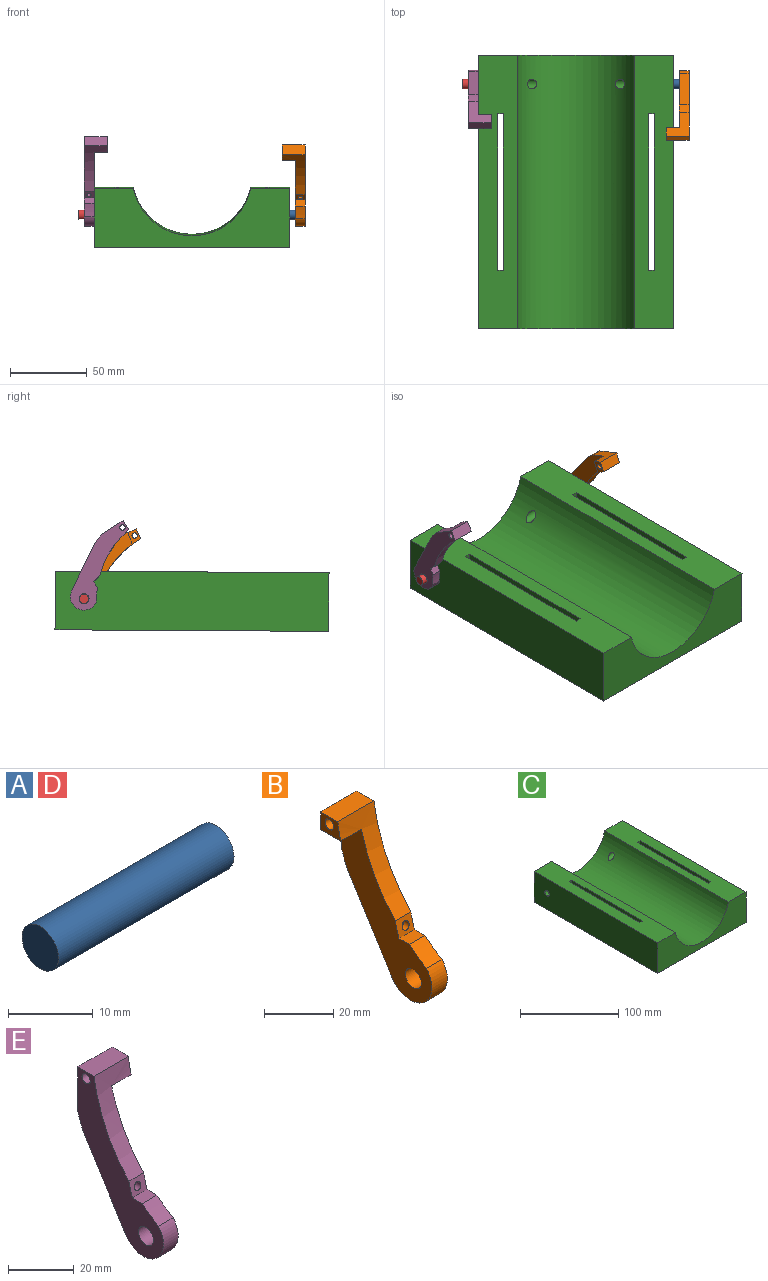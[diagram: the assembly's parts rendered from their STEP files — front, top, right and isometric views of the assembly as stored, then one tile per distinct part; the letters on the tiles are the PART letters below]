
ASSEMBLY  parts=5 mates=8
PART A: 3 faces, bbox 29.2x6.1x6.1 mm
  f0: cylinder r=3.05mm len=29.21mm, axis (1,0,0), area 559.4mm2, adj f1,f2
  f1: plane 6.1x6.1mm, normal (-1,0,0), area 29.2mm2, adj f0
  f2: plane 6.1x6.1mm, normal (1,0,0), area 29.2mm2, adj f0
PART B: 17 faces, bbox 14.8x36.9x56.7 mm
  f0: plane 50.49x36.92mm, normal (-1,0,0), area 667.1mm2, adj f1,f2,f3,f4,f5,f6,f8,f9
  f1: plane 29.6x18.48mm, normal (0,0.85,-0.53), area 221.6mm2, adj f0,f2,f9,f11
  f2: cylinder r=8.73mm len=16.13mm, axis (-1,0,0), area 183mm2, adj f0,f1,f3,f11
  f3: cylinder r=58.9mm len=6.98mm, axis (-1,0,0), area 54.4mm2, adj f0,f2,f4,f11
  f4: plane 6.35x4.29mm, normal (0,0,1), area 27.2mm2, adj f0,f3,f5,f11
  f5: plane 6.35x5.48mm, normal (0,-0.96,0.26), area 29.8mm2, adj f0,f4,f6,f11,f15
  f6: cylinder r=58.9mm len=31.78mm, axis (-1,0,0), area 280.3mm2, adj f0,f5,f7,f11,f12,f13
  f7: plane 14.81x6.96mm, normal (0,0,1), area 103.1mm2, adj f6,f8,f11,f13
  f8: plane 16.75x14.81mm, normal (0,1,0), area 159mm2, adj f0,f7,f9,f11,f12,f13
  f9: cylinder r=54.94mm len=6.35mm, axis (-1,0,0), area 42.4mm2, adj f0,f1,f8,f11
  f10: cylinder r=3.25mm len=6.5mm, axis (-1,0,0), area 129.7mm2, adj f0,f11
  f11: plane 56.71x36.92mm, normal (1,0,0), area 704.2mm2, adj f1,f2,f3,f4,f5,f6,f7,f8
  f12: plane 8.46x8.17mm, normal (0,0,-1), area 69.1mm2, adj f0,f6,f8,f13
  f13: plane 8.17x6.22mm, normal (-1,0,0), area 37mm2, adj f6,f7,f8,f12,f14
  f14: cylinder r=1.76mm len=14.81mm, axis (-1,0,0), area 163.6mm2, adj f11,f13
  f15: cylinder r=1.4mm len=2.79mm, axis (0,-1,0), area 17.3mm2, adj f5,f16
  f16: plane 2.79x2.79mm, normal (0,-1,0), area 6.1mm2, adj f15
PART C: 18 faces, bbox 127x177.8x38.1 mm
  f0: plane 177.8x127mm, normal (0,0,-1), area 21835mm2, adj f2,f3,f4,f6,f7,f8,f9,f12
  f1: plane 177.8x25.4mm, normal (0,0,1), area 4143.3mm2, adj f2,f3,f4,f5,f6,f7,f8,f9
  f2: plane 127x38.1mm, normal (0,-1,0), area 3099mm2, adj f0,f1,f4,f5,f11,f12
  f3: plane 127x38.1mm, normal (0,1,0), area 3099mm2, adj f0,f1,f4,f5,f11,f12
  f4: plane 177.8x38.1mm, normal (-1,0,0), area 6742.5mm2, adj f0,f1,f2,f3,f10
  f5: cylinder r=39.02mm len=177.8mm, axis (0,-1,0), area 18691.8mm2, adj f1,f2,f3,f10,f11,f17
  f6: plane 38.1x3.67mm, normal (0,-1,0), area 139.8mm2, adj f0,f1,f7,f9
  f7: plane 101.6x38.1mm, normal (1,0,0), area 3871mm2, adj f0,f1,f6,f8
  f8: plane 38.1x3.67mm, normal (0,1,0), area 139.8mm2, adj f0,f1,f7,f9
  f9: plane 101.6x38.1mm, normal (-1,0,0), area 3871mm2, adj f0,f1,f6,f8
  f10: cylinder r=3.17mm len=37.9mm, axis (1,0,0), area 694.5mm2, adj f4,f5
  f11: plane 177.8x25.4mm, normal (0,0,1), area 4143.3mm2, adj f2,f3,f5,f12,f13,f14,f15,f16
  f12: plane 177.8x38.1mm, normal (1,0,0), area 6742.5mm2, adj f0,f2,f3,f11,f17
  f13: plane 38.1x3.67mm, normal (0,-1,0), area 139.8mm2, adj f0,f11,f14,f16
  f14: plane 101.6x38.1mm, normal (-1,0,0), area 3871mm2, adj f0,f11,f13,f15
  f15: plane 38.1x3.67mm, normal (0,1,0), area 139.8mm2, adj f0,f11,f14,f16
  f16: plane 101.6x38.1mm, normal (1,0,0), area 3871mm2, adj f0,f11,f13,f15
  f17: cylinder r=3.17mm len=37.9mm, axis (-1,0,0), area 694.5mm2, adj f5,f12
PART D: same geometry as A
PART E: 17 faces, bbox 14.8x36.9x56.7 mm
  f0: plane 50.49x36.92mm, normal (1,0,0), area 667.1mm2, adj f1,f2,f3,f4,f5,f6,f8,f9
  f1: plane 29.6x18.48mm, normal (0,0.85,-0.53), area 221.6mm2, adj f0,f2,f9,f11
  f2: cylinder r=8.73mm len=16.13mm, axis (1,0,0), area 183mm2, adj f0,f1,f3,f11
  f3: cylinder r=58.9mm len=6.98mm, axis (1,0,0), area 54.4mm2, adj f0,f2,f4,f11
  f4: plane 6.35x4.29mm, normal (0,0,1), area 27.2mm2, adj f0,f3,f5,f11
  f5: plane 6.35x5.48mm, normal (0,-0.96,0.26), area 29.8mm2, adj f0,f4,f6,f11,f15
  f6: cylinder r=58.9mm len=31.78mm, axis (1,0,0), area 280.3mm2, adj f0,f5,f7,f11,f12,f13
  f7: plane 14.81x6.96mm, normal (0,0,1), area 103.1mm2, adj f6,f8,f11,f13
  f8: plane 16.75x14.81mm, normal (0,1,0), area 159mm2, adj f0,f7,f9,f11,f12,f13
  f9: cylinder r=54.94mm len=6.35mm, axis (1,0,0), area 42.4mm2, adj f0,f1,f8,f11
  f10: cylinder r=3.25mm len=6.5mm, axis (1,0,0), area 129.7mm2, adj f0,f11
  f11: plane 56.71x36.92mm, normal (-1,0,0), area 704.2mm2, adj f1,f2,f3,f4,f5,f6,f7,f8
  f12: plane 8.46x8.17mm, normal (0,0,-1), area 69.1mm2, adj f0,f6,f8,f13
  f13: plane 8.17x6.22mm, normal (1,0,0), area 37mm2, adj f6,f7,f8,f12,f14
  f14: cylinder r=1.76mm len=14.81mm, axis (1,0,0), area 163.6mm2, adj f11,f13
  f15: cylinder r=1.4mm len=2.79mm, axis (0,-1,0), area 17.3mm2, adj f5,f16
  f16: plane 2.79x2.79mm, normal (0,-1,0), area 6.1mm2, adj f15
PLACE A rot(axis=(0,0.8,-0.6),180deg) t=(129.31,51.74,68.67)mm
PLACE B rot(axis=(1,0,0),68.1deg) t=(23.6,44.91,-64.25)mm
PLACE C rot(axis=(1,0,0),0.3deg) t=(9.99,-0.05,-19.54)mm
PLACE D rot(axis=(0,1,0),180deg) t=(11.2,0.01,2.22)mm fixed
PLACE E rot(axis=(1,0,0),57.8deg) t=(0,33.58,-58.69)mm
MATE cylindrical A.f0 <-> B.f10  axis (1,0,0) through (83.65,69.99,1.1)mm
MATE cylindrical E.f10 <-> C.f10  axis (-1,0,0) through (-59.86,69.99,1.1)mm
MATE cylindrical A.f0 <-> C.f17  axis (-1,0,0) through (69.05,69.99,1.1)mm
MATE planar E.f0 <-> C.f4  axis (1,0,0) through (-53.51,63.66,20.14)mm
MATE planar A.f0 <-> C.f17  axis (-1,0,0) through (83.65,69.99,1.1)mm
MATE parallel B.f11 <-> A.f0  axis (1,0,0) through (83.46,59.14,19.9)mm
MATE planar D.f0 <-> C.f10  axis (-1,0,0) through (-63.67,69.99,1.1)mm
MATE cylindrical C.f10 <-> D.f0  axis (-1,0,0) through (-53.51,69.99,1.1)mm
